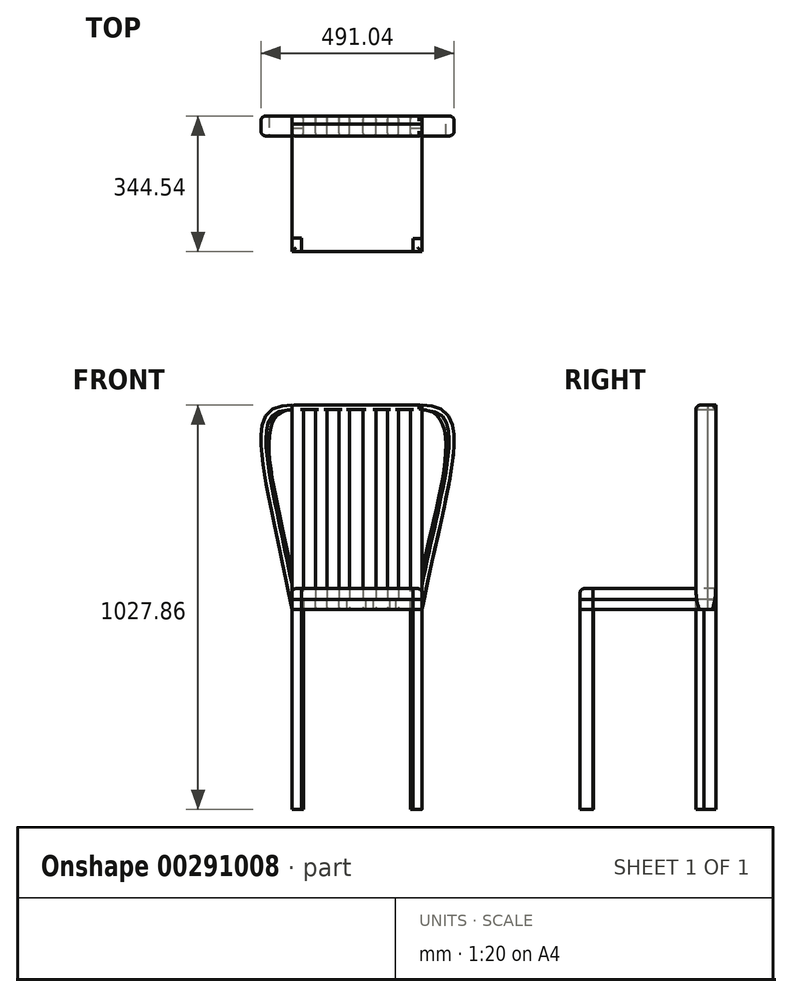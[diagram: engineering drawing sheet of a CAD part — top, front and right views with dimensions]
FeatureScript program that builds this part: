
annotation { "Feature Type Name" : "Feature", "Feature Type Description" : "" }
export const myFeature = defineFeature(function(context is Context, id is Id, definition is map)
    precondition{}
    {
        {
            var Q0;
            Q0=qCreatedBy(makeId("Front.planeOp"),FACE);
            var sketch = newSketch(context, id + "F0", { "sketchPlane" : qUnion([Q0])});
            skLineSegment(sketch, "E0.left", {"start": v(165.1, -508) * mm, "end": v(165.1, 508) * mm});
            skLineSegment(sketch, "E0.right", {"start": v(-165.1, -508) * mm, "end": v(-165.1, 508) * mm});
            skPoint(sketch, "E0.middle", {"position": v(0, 0) * mm});
            skLineSegment(sketch, "E1", {"start": v(-165.1, 0) * mm, "end": v(165.1, 0) * mm});
            skLineSegment(sketch, "E2", {"start": v(-136.2, 0) * mm, "end": v(-136.2, -508) * mm});
            skLineSegment(sketch, "E3", {"start": v(136.12, 0) * mm, "end": v(136.12, -508) * mm});
            skLineSegment(sketch, "E4", {"start": v(136.12, -508) * mm, "end": v(165.1, -508) * mm});
            skLineSegment(sketch, "E5", {"start": v(-165.1, -508) * mm, "end": v(-136.2, -508) * mm});
            skLineSegment(sketch, "E6", {"start": v(-136.2, 0) * mm, "end": v(-136.2, 508) * mm});
            skLineSegment(sketch, "E7", {"start": v(136.12, 0) * mm, "end": v(136.12, 508) * mm});
            skLineSegment(sketch, "E8", {"start": v(105.47, 508) * mm, "end": v(105.47, 0) * mm});
            skLineSegment(sketch, "E9", {"start": v(77.24, 508) * mm, "end": v(77.24, 0) * mm});
            skLineSegment(sketch, "E10", {"start": v(48.55, 508) * mm, "end": v(48.55, 0) * mm});
            skLineSegment(sketch, "E11", {"start": v(15.47, 508) * mm, "end": v(15.47, 0) * mm});
            skLineSegment(sketch, "E12", {"start": v(-18.58, 508) * mm, "end": v(-18.58, 0) * mm});
            skLineSegment(sketch, "E13", {"start": v(-46, 508) * mm, "end": v(-46, 0) * mm});
            skLineSegment(sketch, "E14", {"start": v(-75.41, 508) * mm, "end": v(-75.41, 0) * mm});
            skLineSegment(sketch, "E15", {"start": v(-105.57, 508) * mm, "end": v(-105.57, 0) * mm});
            skLineSegment(sketch, "E16", {"start": v(136.12, 508) * mm, "end": v(165.1, 508) * mm});
            skLineSegment(sketch, "E17", {"start": v(105.47, 508) * mm, "end": v(77.24, 508) * mm});
            skLineSegment(sketch, "E18", {"start": v(48.55, 508) * mm, "end": v(15.47, 508) * mm});
            skLineSegment(sketch, "E19", {"start": v(0, 508) * mm, "end": v(-18.58, 508) * mm});
            skLineSegment(sketch, "E20", {"start": v(-21.94, 508) * mm, "end": v(-46, 508) * mm});
            skLineSegment(sketch, "E21", {"start": v(-105.57, 508) * mm, "end": v(-110.44, 508) * mm});
            skLineSegment(sketch, "E22", {"start": v(-136.2, 508) * mm, "end": v(-165.1, 508) * mm});
            skLineSegment(sketch, "E23", {"start": v(165.1, 508) * mm, "end": v(-165.1, 508) * mm});
            skLineSegment(sketch, "E24", {"start": v(-165.1, 508) * mm, "end": v(-165.1, 519.86) * mm});
            skLineSegment(sketch, "E25", {"start": v(-165.1, 519.86) * mm, "end": v(165.22, 519.86) * mm});
            skLineSegment(sketch, "E26", {"start": v(165.22, 519.86) * mm, "end": v(165.1, 508) * mm});
            skFitSpline(sketch, "E27", {"points": [v(165.22, 519.86) * mm, v(165.1, 0) * mm], "startDerivative": vector(411.26, -5.45) * mm, "endDerivative": vector(-232.62, -1130.36) * mm});
            skFitSpline(sketch, "E28", {"points": [v(-165.1, 519.86) * mm, v(-165.1, 0) * mm], "startDerivative": vector(-397.7, 2.56) * mm, "endDerivative": vector(220.36, -1129.57) * mm});
            skFitSpline(sketch, "E29", {"points": [v(165.1, 508) * mm, v(165.1, 62.2) * mm], "startDerivative": vector(411.13, -13.78) * mm, "endDerivative": vector(0, -363.35) * mm});
            skFitSpline(sketch, "E30", {"points": [v(-165.1, 508) * mm, v(-165.1, 62.2) * mm], "startDerivative": vector(-393.38, -9.45) * mm, "endDerivative": vector(0, -363.35) * mm});
            skSolve(sketch);
        }
        {
            var Q0;
            {var subQ0=sQuery(id+"F0.wireOp",EDGE,"E7");Q0=makeQuery(id+"F0.imprint","IMPRINT",FACE,{"disambiguationData":[TD([[makeQuery(id+"F0.imprint","IMPRINT",EDGE,{"derivedFrom":subQ0}),-1.0]])]});}
            var Q1;
            {var subQ0=sQuery(id+"F0.wireOp",EDGE,"E8");Q1=makeQuery(id+"F0.imprint","IMPRINT",FACE,{"disambiguationData":[TD([[makeQuery(id+"F0.imprint","IMPRINT",EDGE,{"derivedFrom":subQ0}),-1.0]])]});}
            var Q2;
            {var subQ0=sQuery(id+"F0.wireOp",EDGE,"E10");Q2=makeQuery(id+"F0.imprint","IMPRINT",FACE,{"disambiguationData":[TD([[makeQuery(id+"F0.imprint","IMPRINT",EDGE,{"derivedFrom":subQ0}),-1.0]])]});}
            var Q3;
            {var subQ6=sQuery(id+"F0.wireOp",EDGE,"E13");Q3=makeQuery(id+"F0.imprint","IMPRINT",FACE,{"disambiguationData":[TD([[makeQuery(id+"F0.imprint","IMPRINT",EDGE,{"derivedFrom":subQ6}),1.0]])]});}
            var Q4;
            {var subQ0=sQuery(id+"F0.wireOp",EDGE,"E14");Q4=makeQuery(id+"F0.imprint","IMPRINT",FACE,{"disambiguationData":[TD([[makeQuery(id+"F0.imprint","IMPRINT",EDGE,{"derivedFrom":subQ0}),-1.0]])]});}
            var Q5;
            {var subQ0=sQuery(id+"F0.wireOp",EDGE,"E6");Q5=makeQuery(id+"F0.imprint","IMPRINT",FACE,{"disambiguationData":[TD([[makeQuery(id+"F0.imprint","IMPRINT",EDGE,{"derivedFrom":subQ0}),1.0]])]});}
            var Q6;
            {var subQ15=sQuery(id+"F0.wireOp",EDGE,"E24");Q6=makeQuery(id+"F0.imprint","IMPRINT",FACE,{"disambiguationData":[TD([[makeQuery(id+"F0.imprint","IMPRINT",EDGE,{"derivedFrom":subQ15}),-1.0]])]});}
            extrude(context, id + "F1", {"entities" : qUnion([Q0, Q1, Q2, Q3, Q4, Q5, Q6]), "depth" : 20.32 * mm});
        }
        {
            var Q0;
            {var subQ4=sQuery(id+"F0.wireOp",EDGE,"E2");Q0=makeQuery(id+"F0.imprint","IMPRINT",FACE,{"disambiguationData":[TD([[makeQuery(id+"F0.imprint","IMPRINT",EDGE,{"derivedFrom":subQ4}),-1.0]])]});}
            var Q1;
            {var subQ4=sQuery(id+"F0.wireOp",EDGE,"E3");Q1=makeQuery(id+"F0.imprint","IMPRINT",FACE,{"disambiguationData":[TD([[makeQuery(id+"F0.imprint","IMPRINT",EDGE,{"derivedFrom":subQ4}),1.0]])]});}
            extrude(context, id + "F2", {"entities" : qUnion([Q0, Q1]), "operationType" : NewBodyOperationType.ADD, "depth" : 30.48 * mm});
        }
        {
            var Q0;
            Q0=qCreatedBy(makeId("Top.planeOp"),FACE);
            var sketch = newSketch(context, id + "F3", { "sketchPlane" : qUnion([Q0])});
            skLineSegment(sketch, "E31", {"start": v(165.03, 0) * mm, "end": v(165.03, -344.54) * mm});
            skLineSegment(sketch, "E32", {"start": v(-164.99, 0) * mm, "end": v(-164.99, -344.54) * mm});
            skLineSegment(sketch, "E33", {"start": v(-164.99, -344.54) * mm, "end": v(165.03, -344.54) * mm});
            skLineSegment(sketch, "E34", {"start": v(-140.76, 0) * mm, "end": v(-140.76, -344.54) * mm});
            skLineSegment(sketch, "E35", {"start": v(142.5, 0) * mm, "end": v(142.5, -344.54) * mm});
            skLineSegment(sketch, "E36", {"start": v(142.5, -0.19) * mm, "end": v(165.03, -0.19) * mm});
            skLineSegment(sketch, "E37", {"start": v(-164.99, -0.19) * mm, "end": v(-140.76, -0.19) * mm});
            skLineSegment(sketch, "E38", {"start": v(-164.99, -0.19) * mm, "end": v(165.03, -0.19) * mm});
            skLineSegment(sketch, "E39", {"start": v(-164.99, -310.64) * mm, "end": v(-140.76, -310.64) * mm});
            skLineSegment(sketch, "E40", {"start": v(165.03, -312.07) * mm, "end": v(142.5, -312.07) * mm});
            skSolve(sketch);
        }
        {
            var Q0;
            {var subQ4=sQuery(id+"F3.wireOp",EDGE,"E34");var subQ5=sQuery(id+"F3.wireOp",EDGE,"E33");var subQ6=makeQuery(id+"F3.imprint","INTERSECT",VERTEX,{"derivedFrom":[subQ5,subQ4]});Q0=makeQuery(id+"F3.imprint","IMPRINT",FACE,{"disambiguationData":[TD([[makeQuery(id+"F3.imprint","IMPRINT",EDGE,{"disambiguationData":[TD([[subQ6,-1.0]])],"derivedFrom":subQ5}),1.0]])]});}
            var Q1;
            {var subQ3=sQuery(id+"F3.wireOp",EDGE,"E40");Q1=makeQuery(id+"F3.imprint","IMPRINT",FACE,{"disambiguationData":[TD([[makeQuery(id+"F3.imprint","IMPRINT",EDGE,{"derivedFrom":subQ3}),-1.0]])]});}
            var Q2;
            {var subQ3=sQuery(id+"F3.wireOp",EDGE,"E39");Q2=makeQuery(id+"F3.imprint","IMPRINT",FACE,{"disambiguationData":[TD([[makeQuery(id+"F3.imprint","IMPRINT",EDGE,{"derivedFrom":subQ3}),1.0]])]});}
            extrude(context, id + "F4", {"entities" : qUnion([Q0, Q1, Q2]), "operationType" : NewBodyOperationType.ADD, "depth" : 25.4 * mm});
        }
        {
            var Q0;
            {var subQ3=sQuery(id+"F3.wireOp",EDGE,"E40");Q0=makeQuery(id+"F3.imprint","IMPRINT",FACE,{"disambiguationData":[TD([[makeQuery(id+"F3.imprint","IMPRINT",EDGE,{"derivedFrom":subQ3}),1.0]])]});}
            var Q1;
            {var subQ3=sQuery(id+"F3.wireOp",EDGE,"E39");Q1=makeQuery(id+"F3.imprint","IMPRINT",FACE,{"disambiguationData":[TD([[makeQuery(id+"F3.imprint","IMPRINT",EDGE,{"derivedFrom":subQ3}),-1.0]])]});}
            extrude(context, id + "F5", {"entities" : qUnion([Q0, Q1]), "oppositeDirection" : true, "depth" : 508 * mm});
        }
        {
            var Q0;
            {var subQ3=sQuery(id+"F3.wireOp",EDGE,"E39");Q0=makeQuery(id+"F3.imprint","IMPRINT",FACE,{"disambiguationData":[TD([[makeQuery(id+"F3.imprint","IMPRINT",EDGE,{"derivedFrom":subQ3}),-1.0]])]});}
            var Q1;
            {var subQ3=sQuery(id+"F3.wireOp",EDGE,"E40");Q1=makeQuery(id+"F3.imprint","IMPRINT",FACE,{"disambiguationData":[TD([[makeQuery(id+"F3.imprint","IMPRINT",EDGE,{"derivedFrom":subQ3}),1.0]])]});}
            extrude(context, id + "F6", {"entities" : qUnion([Q0, Q1]), "depth" : 25.4 * mm});
        }
        {
            var Q0;
            {var subQ4=sQuery(id+"F3.wireOp",EDGE,"E34");var subQ5=sQuery(id+"F3.wireOp",EDGE,"E33");var subQ6=makeQuery(id+"F3.imprint","INTERSECT",VERTEX,{"derivedFrom":[subQ5,subQ4]});Q0=makeQuery(id+"F3.imprint","IMPRINT",FACE,{"disambiguationData":[TD([[makeQuery(id+"F3.imprint","IMPRINT",EDGE,{"disambiguationData":[TD([[subQ6,-1.0]])],"derivedFrom":subQ5}),1.0]])]});}
            var Q1;
            {var subQ3=sQuery(id+"F3.wireOp",EDGE,"E39");Q1=makeQuery(id+"F3.imprint","IMPRINT",FACE,{"disambiguationData":[TD([[makeQuery(id+"F3.imprint","IMPRINT",EDGE,{"derivedFrom":subQ3}),1.0]])]});}
            var Q2;
            {var subQ3=sQuery(id+"F3.wireOp",EDGE,"E40");Q2=makeQuery(id+"F3.imprint","IMPRINT",FACE,{"disambiguationData":[TD([[makeQuery(id+"F3.imprint","IMPRINT",EDGE,{"derivedFrom":subQ3}),-1.0]])]});}
            extrude(context, id + "F7", {"entities" : qUnion([Q0, Q1, Q2]), "depth" : 53.34 * mm});
        }
        {
            var Q0;
            {var subQ0=sQuery(id+"F0.wireOp",EDGE,"E7");Q0=makeQuery(id+"F0.imprint","IMPRINT",FACE,{"disambiguationData":[TD([[makeQuery(id+"F0.imprint","IMPRINT",EDGE,{"derivedFrom":subQ0}),-1.0]])]});}
            var Q1;
            {var subQ0=sQuery(id+"F0.wireOp",EDGE,"E8");Q1=makeQuery(id+"F0.imprint","IMPRINT",FACE,{"disambiguationData":[TD([[makeQuery(id+"F0.imprint","IMPRINT",EDGE,{"derivedFrom":subQ0}),-1.0]])]});}
            var Q2;
            {var subQ0=sQuery(id+"F0.wireOp",EDGE,"E10");Q2=makeQuery(id+"F0.imprint","IMPRINT",FACE,{"disambiguationData":[TD([[makeQuery(id+"F0.imprint","IMPRINT",EDGE,{"derivedFrom":subQ0}),-1.0]])]});}
            var Q3;
            {var subQ6=sQuery(id+"F0.wireOp",EDGE,"E13");Q3=makeQuery(id+"F0.imprint","IMPRINT",FACE,{"disambiguationData":[TD([[makeQuery(id+"F0.imprint","IMPRINT",EDGE,{"derivedFrom":subQ6}),1.0]])]});}
            var Q4;
            {var subQ0=sQuery(id+"F0.wireOp",EDGE,"E14");Q4=makeQuery(id+"F0.imprint","IMPRINT",FACE,{"disambiguationData":[TD([[makeQuery(id+"F0.imprint","IMPRINT",EDGE,{"derivedFrom":subQ0}),-1.0]])]});}
            var Q5;
            {var subQ0=sQuery(id+"F0.wireOp",EDGE,"E6");Q5=makeQuery(id+"F0.imprint","IMPRINT",FACE,{"disambiguationData":[TD([[makeQuery(id+"F0.imprint","IMPRINT",EDGE,{"derivedFrom":subQ0}),1.0]])]});}
            var Q6;
            {var subQ15=sQuery(id+"F0.wireOp",EDGE,"E24");Q6=makeQuery(id+"F0.imprint","IMPRINT",FACE,{"disambiguationData":[TD([[makeQuery(id+"F0.imprint","IMPRINT",EDGE,{"derivedFrom":subQ15}),-1.0]])]});}
            extrude(context, id + "F8", {"entities" : qUnion([Q0, Q1, Q2, Q3, Q4, Q5, Q6]), "depth" : 50.8 * mm});
        }
        {
            var Q0;
            {var subQ4=sQuery(id+"F0.wireOp",EDGE,"E3");Q0=makeQuery(id+"F0.imprint","IMPRINT",FACE,{"disambiguationData":[TD([[makeQuery(id+"F0.imprint","IMPRINT",EDGE,{"derivedFrom":subQ4}),1.0]])]});}
            var Q1;
            {var subQ4=sQuery(id+"F0.wireOp",EDGE,"E2");Q1=makeQuery(id+"F0.imprint","IMPRINT",FACE,{"disambiguationData":[TD([[makeQuery(id+"F0.imprint","IMPRINT",EDGE,{"derivedFrom":subQ4}),-1.0]])]});}
            extrude(context, id + "F9", {"entities" : qUnion([Q0, Q1]), "depth" : 50.8 * mm});
        }
        {
            var Q0;
            {var subQ3=sQuery(id+"F3.wireOp",EDGE,"E39");Q0=makeQuery(id+"F3.imprint","IMPRINT",FACE,{"disambiguationData":[TD([[makeQuery(id+"F3.imprint","IMPRINT",EDGE,{"derivedFrom":subQ3}),-1.0]])]});}
            var Q1;
            {var subQ3=sQuery(id+"F3.wireOp",EDGE,"E40");Q1=makeQuery(id+"F3.imprint","IMPRINT",FACE,{"disambiguationData":[TD([[makeQuery(id+"F3.imprint","IMPRINT",EDGE,{"derivedFrom":subQ3}),1.0]])]});}
            extrude(context, id + "F10", {"entities" : qUnion([Q0, Q1]), "depth" : 53.34 * mm});
        }
        {
            var Q0;
            Q0=makeQuery(id+"F0.imprint","IMPRINT",FACE,{"disambiguationData":[TD([[makeQuery(id+"F0.imprint","IMPRINT",EDGE,{"derivedFrom":sQuery(id+"F0.wireOp",EDGE,"E24")}),1.0]])]});
            var Q1;
            Q1=makeQuery(id+"F0.imprint","IMPRINT",FACE,{"disambiguationData":[TD([[makeQuery(id+"F0.imprint","IMPRINT",EDGE,{"derivedFrom":sQuery(id+"F0.wireOp",EDGE,"E26")}),1.0]])]});
            extrude(context, id + "F11", {"entities" : qUnion([Q0, Q1]), "depth" : 50.8 * mm});
        }
        {
            var Q0;
            Q0=makeQuery(id+"F11.opExtrude","CAP_EDGE",EDGE,{"disambiguationData":[OSD([sQuery(id+"F0.wireOp",EDGE,"E27")])],"isStart":false});
            var Q1;
            Q1=makeQuery(id+"F11.opExtrude","CAP_EDGE",EDGE,{"disambiguationData":[OSD([sQuery(id+"F0.wireOp",EDGE,"E28")])],"isStart":false});
            var Q2;
            Q2=makeQuery(id+"F11.opExtrude","CAP_EDGE",EDGE,{"disambiguationData":[OSD([sQuery(id+"F0.wireOp",EDGE,"E28")])],"isStart":true});
            var Q3;
            Q3=makeQuery(id+"F11.opExtrude","CAP_EDGE",EDGE,{"disambiguationData":[OSD([sQuery(id+"F0.wireOp",EDGE,"E27")])],"isStart":true});
            var Q4;
            Q4=makeQuery(id+"F8.opExtrude","CAP_EDGE",EDGE,{"disambiguationData":[OSD([sQuery(id+"F0.wireOp",EDGE,"E25")])],"isStart":false});
            var Q5;
            Q5=makeQuery(id+"F1.opExtrude","CAP_EDGE",EDGE,{"disambiguationData":[OSD([sQuery(id+"F0.wireOp",EDGE,"E25")])],"isStart":true});
            fillet(context, id + "F12", {"entities" : qUnion([Q0, Q1, Q2, Q3, Q4, Q5]), "radius" : 12.7 * mm, "tangentPropagation" : true, "allowEdgeOverflow" : false});
        }
        {
            var Q0;
            Q0=makeQuery(id+"F8.opExtrude","CAP_EDGE",EDGE,{"disambiguationData":[OSD([sQuery(id+"F0.wireOp",EDGE,"E0.right"),sQuery(id+"F0.wireOp",EDGE,"E24")])],"isStart":false});
            var Q1;
            Q1=makeQuery(id+"F8.opExtrude","CAP_EDGE",EDGE,{"disambiguationData":[OSD([sQuery(id+"F0.wireOp",EDGE,"E6")])],"isStart":false});
            var Q2;
            Q2=makeQuery(id+"F8.opExtrude","CAP_EDGE",EDGE,{"disambiguationData":[OSD([sQuery(id+"F0.wireOp",EDGE,"E15")])],"isStart":false});
            var Q3;
            Q3=makeQuery(id+"F8.opExtrude","CAP_EDGE",EDGE,{"disambiguationData":[OSD([sQuery(id+"F0.wireOp",EDGE,"E14")])],"isStart":false});
            var Q4;
            Q4=makeQuery(id+"F8.opExtrude","CAP_EDGE",EDGE,{"disambiguationData":[OSD([sQuery(id+"F0.wireOp",EDGE,"E13")])],"isStart":false});
            var Q5;
            Q5=makeQuery(id+"F8.opExtrude","CAP_EDGE",EDGE,{"disambiguationData":[OSD([sQuery(id+"F0.wireOp",EDGE,"E12")])],"isStart":false});
            var Q6;
            Q6=makeQuery(id+"F8.opExtrude","CAP_EDGE",EDGE,{"disambiguationData":[OSD([sQuery(id+"F0.wireOp",EDGE,"E11")])],"isStart":false});
            var Q7;
            Q7=makeQuery(id+"F8.opExtrude","CAP_EDGE",EDGE,{"disambiguationData":[OSD([sQuery(id+"F0.wireOp",EDGE,"E10")])],"isStart":false});
            var Q8;
            Q8=makeQuery(id+"F8.opExtrude","CAP_EDGE",EDGE,{"disambiguationData":[OSD([sQuery(id+"F0.wireOp",EDGE,"E9")])],"isStart":false});
            var Q9;
            Q9=makeQuery(id+"F8.opExtrude","CAP_EDGE",EDGE,{"disambiguationData":[OSD([sQuery(id+"F0.wireOp",EDGE,"E8")])],"isStart":false});
            var Q10;
            Q10=makeQuery(id+"F8.opExtrude","CAP_EDGE",EDGE,{"disambiguationData":[OSD([sQuery(id+"F0.wireOp",EDGE,"E7")])],"isStart":false});
            var Q11;
            Q11=makeQuery(id+"F8.opExtrude","CAP_EDGE",EDGE,{"disambiguationData":[OSD([sQuery(id+"F0.wireOp",EDGE,"E0.left")])],"isStart":false});
            var Q12;
            Q12=makeQuery(id+"F8.opExtrude","CAP_EDGE",EDGE,{"disambiguationData":[OSD([sQuery(id+"F0.wireOp",EDGE,"E0.left")])],"isStart":true});
            var Q13;
            Q13=makeQuery(id+"F8.opExtrude","CAP_EDGE",EDGE,{"disambiguationData":[OSD([sQuery(id+"F0.wireOp",EDGE,"E7")])],"isStart":true});
            var Q14;
            Q14=makeQuery(id+"F1.opExtrude","CAP_EDGE",EDGE,{"disambiguationData":[OSD([sQuery(id+"F0.wireOp",EDGE,"E8")])],"isStart":true});
            var Q15;
            Q15=makeQuery(id+"F1.opExtrude","CAP_EDGE",EDGE,{"disambiguationData":[OSD([sQuery(id+"F0.wireOp",EDGE,"E9")])],"isStart":true});
            var Q16;
            Q16=makeQuery(id+"F1.opExtrude","CAP_EDGE",EDGE,{"disambiguationData":[OSD([sQuery(id+"F0.wireOp",EDGE,"E10")])],"isStart":true});
            var Q17;
            Q17=makeQuery(id+"F1.opExtrude","CAP_EDGE",EDGE,{"disambiguationData":[OSD([sQuery(id+"F0.wireOp",EDGE,"E11")])],"isStart":true});
            var Q18;
            Q18=makeQuery(id+"F1.opExtrude","CAP_EDGE",EDGE,{"disambiguationData":[OSD([sQuery(id+"F0.wireOp",EDGE,"E12")])],"isStart":true});
            var Q19;
            Q19=makeQuery(id+"F8.opExtrude","CAP_EDGE",EDGE,{"disambiguationData":[OSD([sQuery(id+"F0.wireOp",EDGE,"E14")])],"isStart":true});
            var Q20;
            Q20=makeQuery(id+"F8.opExtrude","CAP_EDGE",EDGE,{"disambiguationData":[OSD([sQuery(id+"F0.wireOp",EDGE,"E6")])],"isStart":true});
            var Q21;
            {var subQ0=sQuery(id+"F0.wireOp",EDGE,"E0.right");Q21=makeQuery(id+"F2.boolean.opBoolean","MERGE",EDGE,{"derivedFrom":[makeQuery(id+"F1.opExtrude","CAP_EDGE",EDGE,{"disambiguationData":[OSD([subQ0,sQuery(id+"F0.wireOp",EDGE,"E24")])],"isStart":true}),makeQuery(id+"F2.opExtrude","CAP_EDGE",EDGE,{"disambiguationData":[OSD([subQ0])],"isStart":true})]});}
            fillet(context, id + "F13", {"entities" : qUnion([Q0, Q1, Q2, Q3, Q4, Q5, Q6, Q7, Q8, Q9, Q10, Q11, Q12, Q13, Q14, Q15, Q16, Q17, Q18, Q19, Q20, Q21]), "radius" : 7.62 * mm, "tangentPropagation" : true, "allowEdgeOverflow" : false});
        }
        {
            var Q0;
            Q0=makeQuery(id+"F7.opExtrude","CAP_EDGE",EDGE,{"disambiguationData":[OSD([sQuery(id+"F3.wireOp",EDGE,"E31")])],"isStart":false});
            var Q1;
            Q1=makeQuery(id+"F7.opExtrude","CAP_EDGE",EDGE,{"disambiguationData":[OSD([sQuery(id+"F3.wireOp",EDGE,"E32")])],"isStart":false});
            var Q2;
            Q2=makeQuery(id+"F7.opExtrude","CAP_EDGE",EDGE,{"disambiguationData":[OSD([sQuery(id+"F3.wireOp",EDGE,"E33")])],"isStart":false});
            var Q3;
            {var subQ0=sQuery(id+"F3.wireOp",EDGE,"E33");Q3=makeQuery(id+"F10.opExtrude","CAP_EDGE",EDGE,{"disambiguationData":[OSD([subQ0]),TDD([makeQuery(id+"F3.imprint","IMPRINT",EDGE,{"disambiguationData":[TD([[makeQuery(id+"F3.imprint","INTERSECT",VERTEX,{"derivedFrom":[sQuery(id+"F3.wireOp",EDGE,"E32"),subQ0]}),-1.0]])],"derivedFrom":subQ0})])],"isStart":false});}
            var Q4;
            Q4=makeQuery(id+"F10.opExtrude","CAP_EDGE",EDGE,{"disambiguationData":[OSD([sQuery(id+"F3.wireOp",EDGE,"E32")])],"isStart":false});
            var Q5;
            {var subQ0=sQuery(id+"F3.wireOp",EDGE,"E33");Q5=makeQuery(id+"F10.opExtrude","CAP_EDGE",EDGE,{"disambiguationData":[OSD([subQ0]),TDD([makeQuery(id+"F3.imprint","IMPRINT",EDGE,{"disambiguationData":[TD([[makeQuery(id+"F3.imprint","INTERSECT",VERTEX,{"derivedFrom":[sQuery(id+"F3.wireOp",EDGE,"E31"),subQ0]}),1.0]])],"derivedFrom":subQ0})])],"isStart":false});}
            var Q6;
            Q6=makeQuery(id+"F10.opExtrude","CAP_EDGE",EDGE,{"disambiguationData":[OSD([sQuery(id+"F3.wireOp",EDGE,"E31")])],"isStart":false});
            fillet(context, id + "F14", {"entities" : qUnion([Q0, Q1, Q2, Q3, Q4, Q5, Q6]), "radius" : 10.16 * mm, "tangentPropagation" : true, "allowEdgeOverflow" : false});
        }
        {
            var Q0;
            Q0=makeQuery(id+"F5.opExtrude","SWEPT_EDGE",EDGE,{"disambiguationData":[OSD([sQuery(id+"F3.wireOp",EDGE,"E33"),sQuery(id+"F3.wireOp",EDGE,"E35")])]});
            var Q1;
            Q1=makeQuery(id+"F5.opExtrude","SWEPT_EDGE",EDGE,{"disambiguationData":[OSD([sQuery(id+"F3.wireOp",EDGE,"E31"),sQuery(id+"F3.wireOp",EDGE,"E33")])]});
            var Q2;
            Q2=makeQuery(id+"F5.opExtrude","SWEPT_EDGE",EDGE,{"disambiguationData":[OSD([sQuery(id+"F3.wireOp",EDGE,"E31"),sQuery(id+"F3.wireOp",EDGE,"E40")])]});
            var Q3;
            Q3=makeQuery(id+"F9.opExtrude","CAP_EDGE",EDGE,{"disambiguationData":[OSD([sQuery(id+"F0.wireOp",EDGE,"E0.left")])],"isStart":false});
            var Q4;
            Q4=makeQuery(id+"F5.opExtrude","SWEPT_EDGE",EDGE,{"disambiguationData":[OSD([sQuery(id+"F3.wireOp",EDGE,"E33"),sQuery(id+"F3.wireOp",EDGE,"E34")])]});
            var Q5;
            Q5=makeQuery(id+"F5.opExtrude","SWEPT_EDGE",EDGE,{"disambiguationData":[OSD([sQuery(id+"F3.wireOp",EDGE,"E32"),sQuery(id+"F3.wireOp",EDGE,"E33")])]});
            var Q6;
            Q6=makeQuery(id+"F5.opExtrude","SWEPT_EDGE",EDGE,{"disambiguationData":[OSD([sQuery(id+"F3.wireOp",EDGE,"E32"),sQuery(id+"F3.wireOp",EDGE,"E39")])]});
            var Q7;
            Q7=makeQuery(id+"F9.opExtrude","CAP_EDGE",EDGE,{"disambiguationData":[OSD([sQuery(id+"F0.wireOp",EDGE,"E0.right")])],"isStart":true});
            var Q8;
            Q8=makeQuery(id+"F9.opExtrude","CAP_EDGE",EDGE,{"disambiguationData":[OSD([sQuery(id+"F0.wireOp",EDGE,"E0.right")])],"isStart":false});
            var Q9;
            Q9=makeQuery(id+"F9.opExtrude","CAP_EDGE",EDGE,{"disambiguationData":[OSD([sQuery(id+"F0.wireOp",EDGE,"E2")])],"isStart":true});
            var Q10;
            Q10=makeQuery(id+"F9.opExtrude","CAP_EDGE",EDGE,{"disambiguationData":[OSD([sQuery(id+"F0.wireOp",EDGE,"E3")])],"isStart":true});
            var Q11;
            {var subQ0=sQuery(id+"F0.wireOp",EDGE,"E0.left");Q11=makeQuery(id+"F2.boolean.opBoolean","MERGE",EDGE,{"derivedFrom":[makeQuery(id+"F1.opExtrude","CAP_EDGE",EDGE,{"disambiguationData":[OSD([subQ0])],"isStart":true}),makeQuery(id+"F2.opExtrude","CAP_EDGE",EDGE,{"disambiguationData":[OSD([subQ0])],"isStart":true})]});}
            fillet(context, id + "F15", {"entities" : qUnion([Q0, Q1, Q2, Q3, Q4, Q5, Q6, Q7, Q8, Q9, Q10, Q11]), "radius" : 7.62 * mm, "tangentPropagation" : true, "allowEdgeOverflow" : false});
        }
    });
